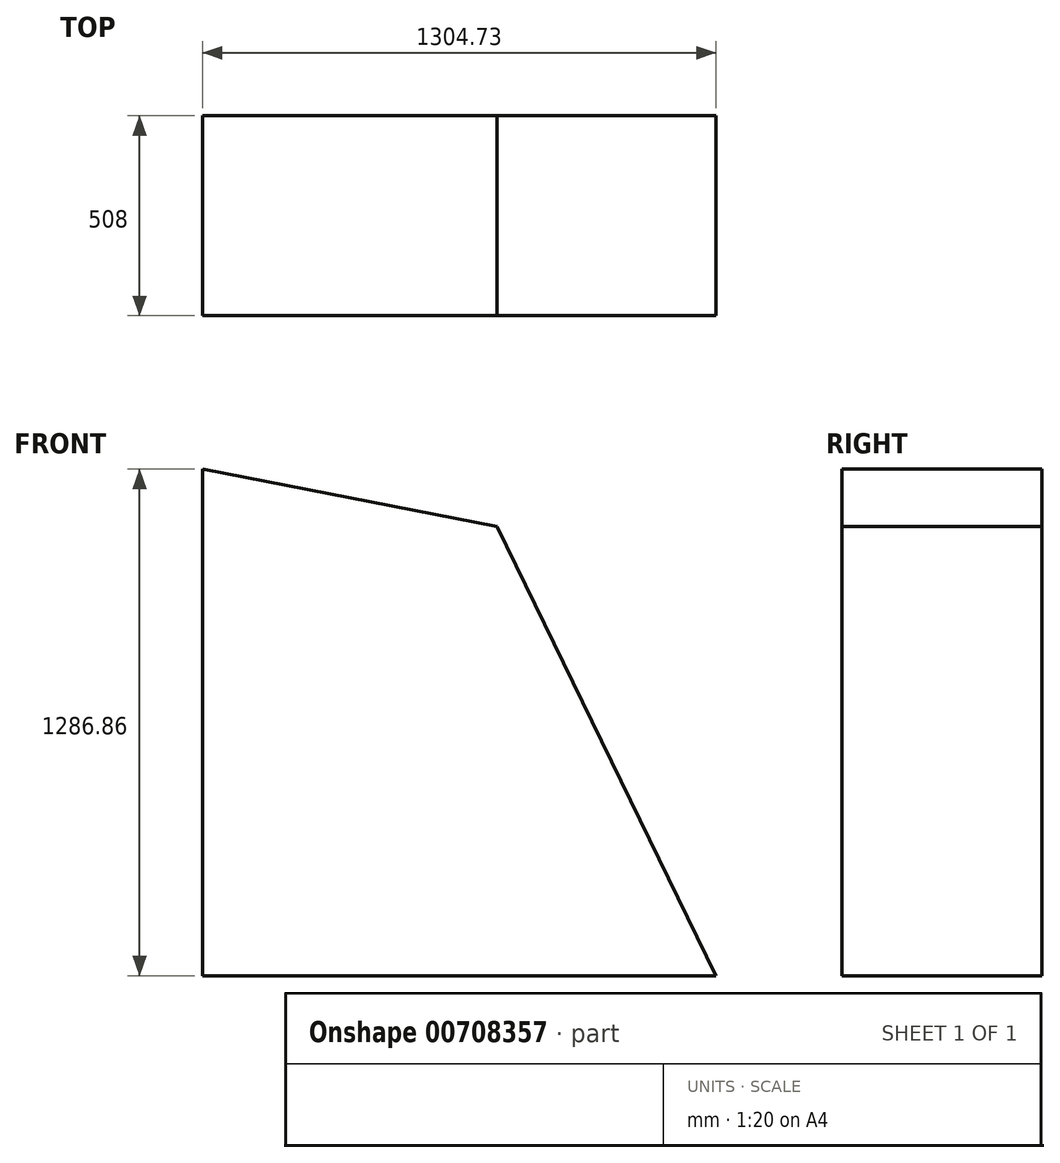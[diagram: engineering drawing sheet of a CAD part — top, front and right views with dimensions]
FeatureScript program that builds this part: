
annotation { "Feature Type Name" : "Feature", "Feature Type Description" : "" }
export const myFeature = defineFeature(function(context is Context, id is Id, definition is map)
    precondition{}
    {
        {
            var Q0;
            Q0=qCreatedBy(makeId("Front.planeOp"),FACE);
            var sketch = newSketch(context, id + "F0", { "sketchPlane" : qUnion([Q0])});
            skLineSegment(sketch, "E0", {"start": v(0, 0) * mm, "end": v(1304.73, 0) * mm});
            skLineSegment(sketch, "E1", {"start": v(1304.73, 0) * mm, "end": v(748, 1141.47) * mm});
            skLineSegment(sketch, "E2", {"start": v(748, 1141.47) * mm, "end": v(0, 1286.86) * mm});
            skLineSegment(sketch, "E3", {"start": v(0, 1286.86) * mm, "end": v(0, 0) * mm});
            skSolve(sketch);
        }
        {
            var Q0;
            Q0=makeQuery(id+"F0.imprint","IMPRINT",FACE,{"disambiguationData":[TD([[makeQuery(id+"F0.imprint","IMPRINT",EDGE,{"derivedFrom":sQuery(id+"F0.wireOp",EDGE,"E0")}),1.0]])]});
            extrude(context, id + "F1", {"entities" : qUnion([Q0]), "depth" : 508 * mm, "offsetDistance" : 25.4 * mm});
        }
    });
